# Revit family: 44870180
name_source: partatom
category: Plumbing Fixtures
revit_build: Autodesk Revit 2016 (Build: 20150220_1215(x64)
units: mm (PartAtom-declared; Revit-internal decimal feet)

## family parameters
Always vertical = Yes
Cut with Voids When Loaded = No
OmniClass Number = 23.45.55.00
OmniClass Title = Sanitary Faucets, Wastes
Part Type = Normal
Room Calculation Point = No
Round Connector Dimension = Use Diameter
Shared = No
Work Plane-Based = No

## types (1)
- 44870180 Shower faucet with shower set, 230/12 V
    2D/3D/BIM Files URL = http://static.hansa.com
    AssetType = Fixed
    BIMObjectName = 44870180
    BodyMaterial = Brass
    Brand = Hansa
    Catalog Drawing URL = http://static.hansa.com
    Category = Bathroom, shower
    Class = Trim kit
    CloseOffRating = 0
    Color = Chrome
    ControlsNominalDepth = 68 mm
    ControlsNominalHeight = 75 mm
    ControlsNominalWidth = 175 mm
    ConvergoRefNr = 0087-1809-0079-FI
    Customs Code = 84818011
    DN Size = DN15
    Dimension Drawing URL = http://static.hansa.com
    DurationUnit = Year
    EAN Number = 4015474279933
    EMC Directive = 2004/108/EY
    Electrical Connection = 230 / 12 V
    Electronic Parts = Control unit
    FDV Document URL = http://www.hansa.com
    FaucetMainMaterial = Brass
    Features = Trim kit
    Filling Time = 10 min (0 - 20 min)
    Finish = Polished
    FlowCoefficient = 0
    Group = Shower faucets
    HandShowerNominalDepth = 259 mm
    HandShowerNominalHeight = 1096 mm
    HandShowerNominalWidth = 175 mm
    IfcExportAs = IfcValveType
    IfcExportType = FAUCET
    Installation Type = Wall-mounted concealed
    Installation and Maintenance = http://static.hansa.com
    ManufacterURL = http://www.hansa.com
    Manufacturer = Hansa
    ManufacturerName = Hansa
    Market = AUT;BEL;CZE;DEU;ESP;FRA;INT;ITA;NLD;SVK
    Material = Brass
    Max Flow Period = 480.0 s
    Model = 44870180 Shower faucet with shower set, 230/12 V
    ModelReference = 44870180
    NBSDescription = Water supply fittings for wash basins and troughs
    NBSReference = 45-35-70/371
    Name = 44870180 Shower faucet with shower set, 230/12 V
    Name_en = 44870180 Shower faucet with shower set, 230/12 V
    Operating Voltage = 12 V
    Package Weight = 5.5 kg
    Package external Dimensions = 1184 x 325 x 199
    Product Code = 44870180
    Product Datasheet = http://www.hansa.com
    Product Family = HANSALIVING
    Product Image URL = http://static.hansa.com
    Product URL = http://static.hansa.com
    Protection Class = IP 55 / transformer IP 40
    Revision = 2
    Shape = Sculptured
    Size = Controls: 175x70x75 mm / Hand shower: 175x260x1100 mm
    Technology Sales Arguments = The right product for the modular and design-oriented concealed installation system HANSAMATRIX.
    Temperature = Thermostatic temperature control
    Uniclass2 = Pr_40_30_96_07
    Uniclass2015Description = Bath manual water supply sets
    Uniclass2015Reference = Pr_40_20_87_07
    Version = 2
    VersionDate = 01/01/2019
    WarrantyDescription = http://warranty.hansa.com
    WarrantyDurationUnit = Year

## geometry (parser evidence)
native form markers: Sweep x10
no freeform markers — native parametric forms only
